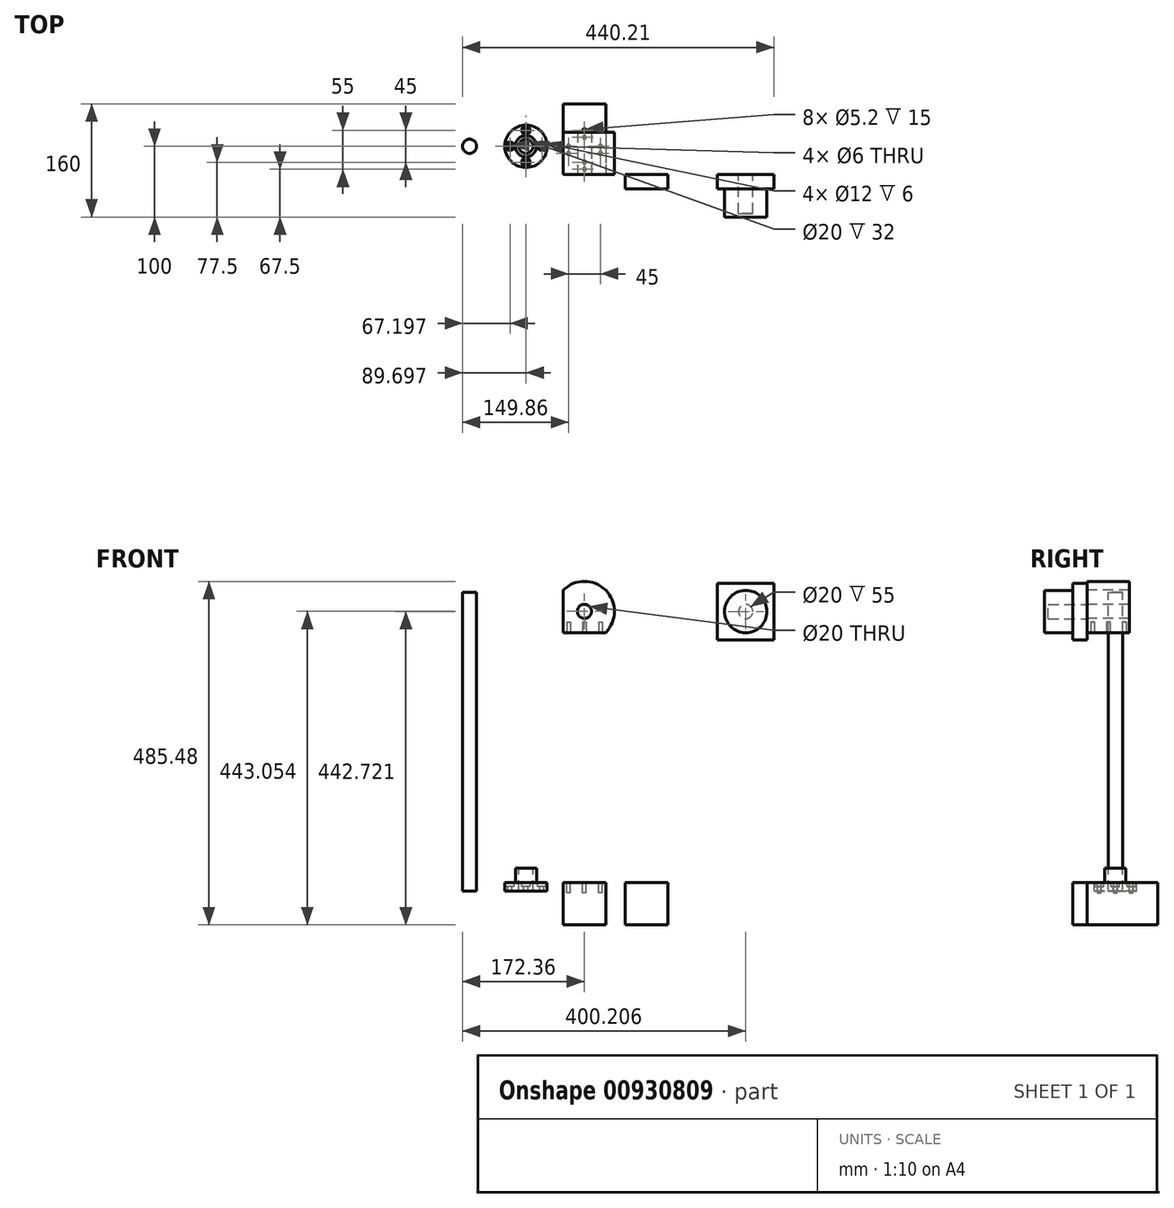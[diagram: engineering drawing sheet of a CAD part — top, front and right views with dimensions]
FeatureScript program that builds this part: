
annotation { "Feature Type Name" : "Feature", "Feature Type Description" : "" }
export const myFeature = defineFeature(function(context is Context, id is Id, definition is map)
    precondition{}
    {
        {
            var Q0;
            Q0=qCreatedBy(makeId("Front.planeOp"),FACE);
            var sketch = newSketch(context, id + "F0", { "sketchPlane" : qUnion([Q0])});
            skLineSegment(sketch, "E0.bottom", {"start": v(-30, 30) * mm, "end": v(30, 30) * mm});
            skLineSegment(sketch, "E0.top", {"start": v(-30, -30) * mm, "end": v(30, -30) * mm});
            skLineSegment(sketch, "E0.left", {"start": v(-30, 30) * mm, "end": v(-30, -30) * mm});
            skLineSegment(sketch, "E0.right", {"start": v(30, 30) * mm, "end": v(30, -30) * mm});
            skPoint(sketch, "E0.middle", {"position": v(0, 0) * mm});
            skSolve(sketch);
        }
        {
            var Q0;
            Q0 = qSketchRegion(id + "F0", true);
            extrude(context, id + "F1", {"entities" : qUnion([Q0]), "oppositeDirection" : true, "depth" : 100 * mm, "offsetDistance" : 25 * mm});
        }
        {
            var Q0;
            Q0=qCreatedBy(makeId("Front.planeOp"),FACE);
            var sketch = newSketch(context, id + "F2", { "sketchPlane" : qUnion([Q0])});
            skLineSegment(sketch, "E1.bottom", {"start": v(57.88, 30) * mm, "end": v(117.88, 30) * mm});
            skLineSegment(sketch, "E1.top", {"start": v(57.88, -30) * mm, "end": v(117.88, -30) * mm});
            skLineSegment(sketch, "E1.left", {"start": v(57.88, 30) * mm, "end": v(57.88, -30) * mm});
            skLineSegment(sketch, "E1.right", {"start": v(117.88, 30) * mm, "end": v(117.88, -30) * mm});
            skPoint(sketch, "E1.middle", {"position": v(87.88, 0) * mm});
            skSolve(sketch);
        }
        {
            var Q0;
            Q0 = qSketchRegion(id + "F2", true);
            extrude(context, id + "F3", {"entities" : qUnion([Q0]), "depth" : 20 * mm, "offsetDistance" : 25 * mm});
        }
        {
            var Q0;
            Q0=makeQuery(id+"F1.opExtrude","SWEPT_FACE",FACE,{"disambiguationData":[OSD([sQuery(id+"F0.wireOp",EDGE,"E0.bottom")])]});
            var sketch = newSketch(context, id + "F4", { "sketchPlane" : qUnion([Q0])});
            skCircle(sketch, "E2", {"center": v(-82.66, 40) * mm, "radius": 30 * mm});
            skPoint(sketch, "E2.centerSnap0", {"position": v(-30, 40) * mm});
            skCircle(sketch, "E3", {"center": v(-82.66, 40) * mm, "radius": 10 * mm});
            skCircle(sketch, "E4", {"center": v(-82.66, 40) * mm, "radius": 15 * mm});
            skCircle(sketch, "E5", {"center": v(-82.66, 62.5) * mm, "radius": 3 * mm});
            skCircle(sketch, "E6.1.0", {"center": v(-105.16, 40) * mm, "radius": 3 * mm});
            skCircle(sketch, "E6.2.0", {"center": v(-82.66, 17.5) * mm, "radius": 3 * mm});
            skCircle(sketch, "E6.3.0", {"center": v(-60.16, 40) * mm, "radius": 3 * mm});
            skCircle(sketch, "E7", {"center": v(-82.66, 62.5) * mm, "radius": 6 * mm});
            skCircle(sketch, "E8", {"center": v(-60.16, 40) * mm, "radius": 6 * mm});
            skCircle(sketch, "E9", {"center": v(-82.66, 17.5) * mm, "radius": 6 * mm});
            skCircle(sketch, "E10", {"center": v(-105.16, 40) * mm, "radius": 6 * mm});
            skCircle(sketch, "E11", {"center": v(0, 62.5) * mm, "radius": 2.6 * mm});
            skCircle(sketch, "E12.1.0", {"center": v(-22.5, 40) * mm, "radius": 2.6 * mm});
            skCircle(sketch, "E12.2.0", {"center": v(0, 17.5) * mm, "radius": 2.6 * mm});
            skCircle(sketch, "E12.3.0", {"center": v(22.5, 40) * mm, "radius": 2.6 * mm});
            skPoint(sketch, "E12.center", {"position": v(0, 40) * mm});
            skCircle(sketch, "E13", {"center": v(-162.36, 40) * mm, "radius": 10 * mm});
            skSolve(sketch);
        }
        {
            var Q0;
            Q0=makeQuery(id+"F4.imprint","IMPRINT",FACE,{"disambiguationData":[TD([[makeQuery(id+"F4.imprint","IMPRINT",EDGE,{"derivedFrom":sQuery(id+"F4.wireOp",EDGE,"E2")}),1.0]])]});
            var Q1;
            Q1=makeQuery(id+"F4.imprint","IMPRINT",FACE,{"disambiguationData":[TD([[makeQuery(id+"F4.imprint","IMPRINT",EDGE,{"derivedFrom":sQuery(id+"F4.wireOp",EDGE,"E6.1.0")}),-1.0]])]});
            var Q2;
            Q2=makeQuery(id+"F4.imprint","IMPRINT",FACE,{"disambiguationData":[TD([[makeQuery(id+"F4.imprint","IMPRINT",EDGE,{"derivedFrom":sQuery(id+"F4.wireOp",EDGE,"E3")}),-1.0]])]});
            var Q3;
            Q3=makeQuery(id+"F4.imprint","IMPRINT",FACE,{"disambiguationData":[TD([[makeQuery(id+"F4.imprint","IMPRINT",EDGE,{"derivedFrom":sQuery(id+"F4.wireOp",EDGE,"E5")}),-1.0]])]});
            var Q4;
            Q4=makeQuery(id+"F4.imprint","IMPRINT",FACE,{"disambiguationData":[TD([[makeQuery(id+"F4.imprint","IMPRINT",EDGE,{"derivedFrom":sQuery(id+"F4.wireOp",EDGE,"E6.3.0")}),-1.0]])]});
            var Q5;
            Q5=makeQuery(id+"F4.imprint","IMPRINT",FACE,{"disambiguationData":[TD([[makeQuery(id+"F4.imprint","IMPRINT",EDGE,{"derivedFrom":sQuery(id+"F4.wireOp",EDGE,"E6.2.0")}),-1.0]])]});
            var Q6;
            Q6=makeQuery(id+"F4.imprint","IMPRINT",FACE,{"disambiguationData":[TD([[makeQuery(id+"F4.imprint","IMPRINT",EDGE,{"derivedFrom":sQuery(id+"F4.wireOp",EDGE,"E2")}),1.0]])]});
            var Q7;
            Q7=makeQuery(id+"F4.imprint","IMPRINT",FACE,{"disambiguationData":[TD([[makeQuery(id+"F4.imprint","IMPRINT",EDGE,{"derivedFrom":sQuery(id+"F4.wireOp",EDGE,"E13")}),1.0]])]});
            extrude(context, id + "F5", {"entities" : qUnion([Q0, Q1, Q2, Q3, Q4, Q5, Q6, Q7]), "oppositeDirection" : true, "depth" : 12 * mm, "offsetDistance" : 25 * mm});
        }
        {
            var Q0;
            Q0=makeQuery(id+"F4.imprint","IMPRINT",FACE,{"disambiguationData":[TD([[makeQuery(id+"F4.imprint","IMPRINT",EDGE,{"derivedFrom":sQuery(id+"F4.wireOp",EDGE,"E5")}),-1.0]])]});
            var Q1;
            Q1=makeQuery(id+"F4.imprint","IMPRINT",FACE,{"disambiguationData":[TD([[makeQuery(id+"F4.imprint","IMPRINT",EDGE,{"derivedFrom":sQuery(id+"F4.wireOp",EDGE,"E6.3.0")}),-1.0]])]});
            var Q2;
            Q2=makeQuery(id+"F4.imprint","IMPRINT",FACE,{"disambiguationData":[TD([[makeQuery(id+"F4.imprint","IMPRINT",EDGE,{"derivedFrom":sQuery(id+"F4.wireOp",EDGE,"E6.2.0")}),-1.0]])]});
            var Q3;
            Q3=makeQuery(id+"F4.imprint","IMPRINT",FACE,{"disambiguationData":[TD([[makeQuery(id+"F4.imprint","IMPRINT",EDGE,{"derivedFrom":sQuery(id+"F4.wireOp",EDGE,"E6.1.0")}),-1.0]])]});
            extrude(context, id + "F6", {"entities" : qUnion([Q0, Q1, Q2, Q3]), "operationType" : NewBodyOperationType.REMOVE, "oppositeDirection" : true, "depth" : 6 * mm, "offsetDistance" : 25 * mm});
        }
        {
            var Q0;
            Q0=makeQuery(id+"F4.imprint","IMPRINT",FACE,{"disambiguationData":[TD([[makeQuery(id+"F4.imprint","IMPRINT",EDGE,{"derivedFrom":sQuery(id+"F4.wireOp",EDGE,"E3")}),-1.0]])]});
            extrude(context, id + "F7", {"entities" : qUnion([Q0]), "operationType" : NewBodyOperationType.ADD, "depth" : 20 * mm, "offsetDistance" : 25 * mm});
        }
        {
            var Q0;
            Q0=makeQuery(id+"F4.imprint","IMPRINT",FACE,{"disambiguationData":[TD([[makeQuery(id+"F4.imprint","IMPRINT",EDGE,{"derivedFrom":sQuery(id+"F4.wireOp",EDGE,"E12.1.0")}),1.0]])]});
            var Q1;
            Q1=makeQuery(id+"F4.imprint","IMPRINT",FACE,{"disambiguationData":[TD([[makeQuery(id+"F4.imprint","IMPRINT",EDGE,{"derivedFrom":sQuery(id+"F4.wireOp",EDGE,"E11")}),1.0]])]});
            var Q2;
            Q2=makeQuery(id+"F4.imprint","IMPRINT",FACE,{"disambiguationData":[TD([[makeQuery(id+"F4.imprint","IMPRINT",EDGE,{"derivedFrom":sQuery(id+"F4.wireOp",EDGE,"E12.2.0")}),1.0]])]});
            var Q3;
            Q3=makeQuery(id+"F4.imprint","IMPRINT",FACE,{"disambiguationData":[TD([[makeQuery(id+"F4.imprint","IMPRINT",EDGE,{"derivedFrom":sQuery(id+"F4.wireOp",EDGE,"E12.3.0")}),1.0]])]});
            extrude(context, id + "F8", {"entities" : qUnion([Q0, Q1, Q2, Q3]), "operationType" : NewBodyOperationType.REMOVE, "oppositeDirection" : true, "depth" : 15 * mm, "offsetDistance" : 25 * mm});
        }
        {
            var Q0;
            Q0=makeQuery(id+"F4.imprint","IMPRINT",FACE,{"disambiguationData":[TD([[makeQuery(id+"F4.imprint","IMPRINT",EDGE,{"derivedFrom":sQuery(id+"F4.wireOp",EDGE,"E13")}),1.0]])]});
            extrude(context, id + "F9", {"entities" : qUnion([Q0]), "operationType" : NewBodyOperationType.ADD, "depth" : 410 * mm, "offsetDistance" : 25 * mm});
        }
        {
            var Q0;
            Q0=qCreatedBy(makeId("Front.planeOp"),FACE);
            var sketch = newSketch(context, id + "F10", { "sketchPlane" : qUnion([Q0])});
            skLineSegment(sketch, "E14.top", {"start": v(-30, 383.05) * mm, "end": v(30, 383.05) * mm});
            skLineSegment(sketch, "E14.left", {"start": v(-30, 443.05) * mm, "end": v(-30, 383.05) * mm});
            skPoint(sketch, "E14.middle", {"position": v(0, 413.05) * mm});
            skCircle(sketch, "E15", {"center": v(0, 413.05) * mm, "radius": 10 * mm});
            skArc(sketch, "E16", {"start": v(30, 383.05) * mm, "mid": v(30, 443.05) * mm, "end": v(-30, 443.05) * mm});
            skPoint(sketch, "E14.bottom.end.orphan", {"position": v(30, 443.05) * mm});
            skSolve(sketch);
        }
        {
            var Q0;
            Q0 = qSketchRegion(id + "F10", true);
            extrude(context, id + "F11", {"entities" : qUnion([Q0]), "oppositeDirection" : true, "depth" : 60 * mm, "offsetDistance" : 25 * mm});
        }
        {
            var Q0;
            Q0=makeQuery(id+"F11.opExtrude","SWEPT_FACE",FACE,{"disambiguationData":[OSD([sQuery(id+"F10.wireOp",EDGE,"E14.top")])]});
            var sketch = newSketch(context, id + "F12", { "sketchPlane" : qUnion([Q0])});
            skCircle(sketch, "E17", {"center": v(0, -7.5) * mm, "radius": 2.6 * mm});
            skCircle(sketch, "E18.1.0", {"center": v(-22.5, -30) * mm, "radius": 2.6 * mm});
            skCircle(sketch, "E18.2.0", {"center": v(0, -52.5) * mm, "radius": 2.6 * mm});
            skCircle(sketch, "E18.3.0", {"center": v(22.5, -30) * mm, "radius": 2.6 * mm});
            skPoint(sketch, "E18.center", {"position": v(0, -30) * mm});
            skSolve(sketch);
        }
        {
            var Q0;
            Q0 = qSketchRegion(id + "F12", true);
            extrude(context, id + "F13", {"entities" : qUnion([Q0]), "operationType" : NewBodyOperationType.REMOVE, "oppositeDirection" : true, "depth" : 15 * mm, "offsetDistance" : 25 * mm});
        }
        {
            var Q0;
            Q0=makeQuery(id+"F11.opExtrude","CAP_FACE",FACE,{"disambiguationData":[OSD([sQuery(id+"F10.wireOp",EDGE,"E14.top"),sQuery(id+"F10.wireOp",EDGE,"E14.left"),sQuery(id+"F10.wireOp",EDGE,"E15"),sQuery(id+"F10.wireOp",EDGE,"E16")])],"isStart":true});
            var sketch = newSketch(context, id + "F14", { "sketchPlane" : qUnion([Q0])});
            skCircle(sketch, "E19", {"center": v(227.85, 412.72) * mm, "radius": 10 * mm});
            skCircle(sketch, "E20", {"center": v(227.85, 412.72) * mm, "radius": 30 * mm});
            skLineSegment(sketch, "E21.bottom", {"start": v(187.85, 452.72) * mm, "end": v(267.85, 452.72) * mm});
            skLineSegment(sketch, "E21.top", {"start": v(187.85, 372.72) * mm, "end": v(267.85, 372.72) * mm});
            skLineSegment(sketch, "E21.left", {"start": v(187.85, 452.72) * mm, "end": v(187.85, 372.72) * mm});
            skLineSegment(sketch, "E21.right", {"start": v(267.85, 452.72) * mm, "end": v(267.85, 372.72) * mm});
            skSolve(sketch);
        }
        {
            var Q0;
            Q0 = qSketchRegion(id + "F14", true);
            var Q1;
            Q1=makeQuery(id+"F14.imprint","IMPRINT",FACE,{"disambiguationData":[TD([[makeQuery(id+"F14.imprint","IMPRINT",EDGE,{"derivedFrom":sQuery(id+"F14.wireOp",EDGE,"E19")}),-1.0]])]});
            var Q2;
            Q2=makeQuery(id+"F14.imprint","IMPRINT",FACE,{"disambiguationData":[TD([[makeQuery(id+"F14.imprint","IMPRINT",EDGE,{"derivedFrom":sQuery(id+"F14.wireOp",EDGE,"E19")}),1.0]])]});
            extrude(context, id + "F15", {"entities" : qUnion([Q0, Q1, Q2]), "depth" : 20 * mm, "offsetDistance" : 25 * mm});
        }
        {
            var Q0;
            Q0=makeQuery(id+"F14.imprint","IMPRINT",FACE,{"disambiguationData":[TD([[makeQuery(id+"F14.imprint","IMPRINT",EDGE,{"derivedFrom":sQuery(id+"F14.wireOp",EDGE,"E19")}),-1.0]])]});
            var Q1;
            Q1=makeQuery(id+"F14.imprint","IMPRINT",FACE,{"disambiguationData":[TD([[makeQuery(id+"F14.imprint","IMPRINT",EDGE,{"derivedFrom":sQuery(id+"F14.wireOp",EDGE,"E19")}),1.0]])]});
            extrude(context, id + "F16", {"entities" : qUnion([Q0, Q1]), "operationType" : NewBodyOperationType.ADD, "depth" : 60 * mm, "offsetDistance" : 25 * mm});
        }
        {
            var Q0;
            Q0=makeQuery(id+"F14.imprint","IMPRINT",FACE,{"disambiguationData":[TD([[makeQuery(id+"F14.imprint","IMPRINT",EDGE,{"derivedFrom":sQuery(id+"F14.wireOp",EDGE,"E19")}),1.0]])]});
            extrude(context, id + "F17", {"entities" : qUnion([Q0]), "operationType" : NewBodyOperationType.REMOVE, "depth" : 55 * mm, "offsetDistance" : 25 * mm});
        }
    });
